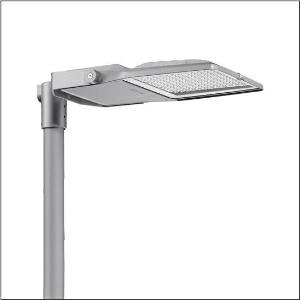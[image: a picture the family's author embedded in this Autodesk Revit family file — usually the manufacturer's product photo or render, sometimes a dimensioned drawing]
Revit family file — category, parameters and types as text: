
# Revit family: floodlight_fl_21_iq_midi___pl52_5xa7782f2d3a_028a
name_source: partatom
category: Lighting Fixtures
units: mm (PartAtom-declared; Revit-internal decimal feet)

## family parameters
Cut with Voids When Loaded = No
Host = Face
Light Source = No
Part Type = Normal
Room Calculation Point = No
Round Connector Dimension = Use Diameter
Shared = No

## types (1)
- --- (1 x LED, 35760 lm, 270.2 W, 3000K)
    Apparent Load = 270 VA
    CIE Flux Codes = 26 60 98 100 100
    Color Rendering = 70
    Color Temperature = 3000K
    Default Elevation = 1800 mm
    Description = Floodlight FL 21 iQ midi, floodlight, primary light control with lens, of PMMA, primary optical cover: protective disc, of toughened safety glass, transparent, light distribution: PL52, light emission: direct distribution, installation type: surface-mounted, LED, High Power LED, rated luminous flux: 35.760lm, luminous efficacy: 132lm/W, light colour: 730, colour temperature: 3000K, control gear: ECG iQ, control: optimised constant luminous flux control (CLO 2.0), Desk-Remote (wireless, voltage-free reading and setting of iQ features in the workshop via application-optimized NFC function/RFID function), Smart-Wire, Night-Set, Temp-Guard, Auto-Match, Street-Remote, with terminal, 6-pole, mains connection: 220..240V, AC, 50/60Hz, start of lifetime: 270W, end of service life: 287W, reduction: 117W, luminaire housing, of diecast aluminium, powder-coated, Siteco® metallic grey (DB 702S), corrosivity category C5 mid according to DIN EN ISO 12944, sealing non-destructively replaceable, please order mast flange separately, mast bracket, of steel, galvanised, powder-coated, Siteco® metallic grey (DB 702S), protection rating (complete): IP66, insulation class (complete): insulation class II (safety insulation), certification: CE, protection symbol: D, impact resistance: IK08, permissible operating ambient temperature: -40..+40°C, permissible operating ambient temperature for outdoor applications: -40..+50°C, standard: DIN EN 12944, LABS conformity tested according to VDMA 24364:2018-05, packaging unit: 1 piece

Light Distribution: PL52
    Height = 76 mm
    Lamp = 1 x LED
    Lamp Light Flux = 35760 lm
    Lamp Power = 270.2 W
    Lamp count = 1
    Length = 657 mm
    Luminous efficacy = 132 lm/W
    Manufacturer = Siteco
    ModVariant = No
    Model = 5XA7782F2D3A
    Number of Poles = 1
    OnlyDefault = Yes
    Power Factor = 1
    Product Name = Floodlight FL 21 iQ midi | PL52
    Product group = floodlight | pylon annexe
    ProductGroupID = 6200
    Protection Class = Protection class II
    Protection Degree = IP 66
    RLX_Detail_Level = 1
    RLX_Emergency_Light_Flux = 0 lm
    RLX_Emergency_Type = 0
    RLX_Emergency_Type_DB = No
    RlxData = <blob elided: 153621 chars, md5=9ea5c496>
    Socket = socket
    Standby Power = 0 W
    System Light Flux = 35760 lm
    System Power = 270 W
    Type Comments = factory setting: luminous flux: 100 % | dim-lin: 254 | 620 mA
    Type Image = l_1007123.jpg
    URL = http://relux.com
    VarID = @adj_053921
    Voltage = 0 V
    Weight = 0.00 kg
    Width = 442 mm

## geometry (parser evidence)
native form markers: Blend x4, Sweep x11
no freeform markers — native parametric forms only
